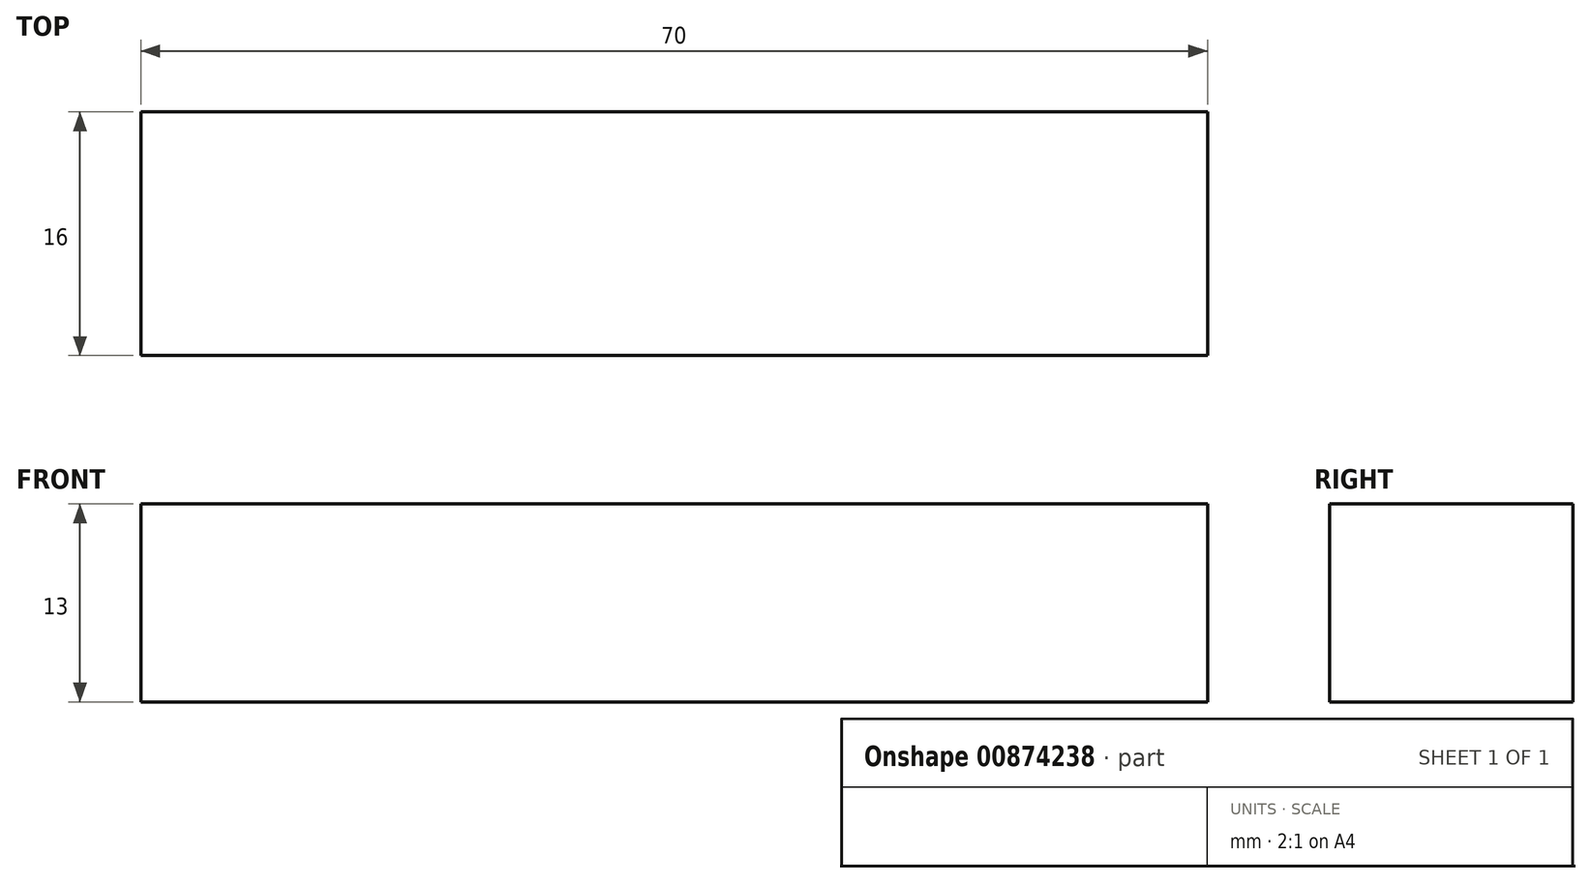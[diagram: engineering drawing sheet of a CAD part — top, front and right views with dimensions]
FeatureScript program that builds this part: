
annotation { "Feature Type Name" : "Feature", "Feature Type Description" : "" }
export const myFeature = defineFeature(function(context is Context, id is Id, definition is map)
    precondition{}
    {
        {
            assignVariable(context, id + "F0", {"name" : "node_height", "anyValue" : 13});
        }
        {
            var Q0;
            Q0=qCreatedBy(makeId("Top.planeOp"),FACE);
            var sketch = newSketch(context, id + "F1", { "sketchPlane" : qUnion([Q0])});
            skLineSegment(sketch, "E0.bottom", {"start": v(35, 8) * mm, "end": v(-35, 8) * mm});
            skLineSegment(sketch, "E0.top", {"start": v(35, -8) * mm, "end": v(-35, -8) * mm});
            skLineSegment(sketch, "E0.left", {"start": v(35, 8) * mm, "end": v(35, -8) * mm});
            skLineSegment(sketch, "E0.right", {"start": v(-35, 8) * mm, "end": v(-35, -8) * mm});
            skPoint(sketch, "E0.middle", {"position": v(0, 0) * mm});
            skSolve(sketch);
        }
        {
            var Q0;
            Q0=makeQuery(id+"F1.imprint","IMPRINT",FACE,{"disambiguationData":[TD([[makeQuery(id+"F1.imprint","IMPRINT",EDGE,{"derivedFrom":sQuery(id+"F1.wireOp",EDGE,"E0.bottom")}),1.0]])]});
            extrude(context, id + "F2", {"entities" : qUnion([Q0]), "depth" : (getVariable(context, 'node_height')) * mm, "offsetDistance" : 25 * mm});
        }
    });
